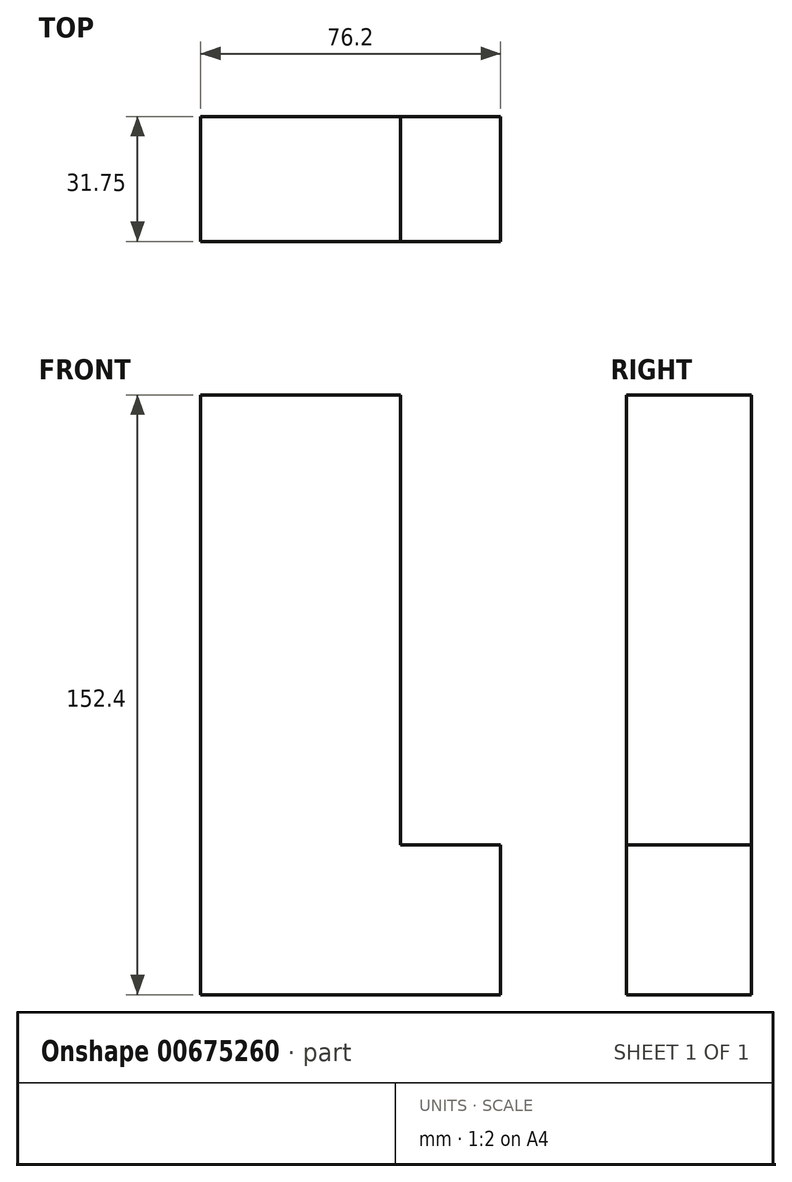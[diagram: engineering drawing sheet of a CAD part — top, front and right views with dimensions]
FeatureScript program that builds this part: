
annotation { "Feature Type Name" : "Feature", "Feature Type Description" : "" }
export const myFeature = defineFeature(function(context is Context, id is Id, definition is map)
    precondition{}
    {
        {
            var Q0;
            Q0=qCreatedBy(makeId("Front.planeOp"),FACE);
            var sketch = newSketch(context, id + "F0", { "sketchPlane" : qUnion([Q0])});
            skLineSegment(sketch, "E0", {"start": v(-75.81, 75.74) * mm, "end": v(-75.81, -76.66) * mm});
            skLineSegment(sketch, "E1", {"start": v(-75.81, -76.66) * mm, "end": v(0.39, -76.66) * mm});
            skLineSegment(sketch, "E2", {"start": v(0.39, -76.66) * mm, "end": v(0.39, -38.56) * mm});
            skLineSegment(sketch, "E3", {"start": v(0.39, -38.56) * mm, "end": v(-25.01, -38.56) * mm});
            skLineSegment(sketch, "E4", {"start": v(-25.01, -38.56) * mm, "end": v(-25.01, 75.74) * mm});
            skLineSegment(sketch, "E5", {"start": v(-25.01, 75.74) * mm, "end": v(-75.81, 75.74) * mm});
            skSolve(sketch);
        }
        {
            var Q0;
            Q0=makeQuery(id+"F0.imprint","IMPRINT",FACE,{"disambiguationData":[TD([[makeQuery(id+"F0.imprint","IMPRINT",EDGE,{"derivedFrom":sQuery(id+"F0.wireOp",EDGE,"E0")}),1.0]])]});
            extrude(context, id + "F1", {"entities" : qUnion([Q0]), "depth" : 31.75 * mm, "offsetDistance" : 25.4 * mm});
        }
    });
